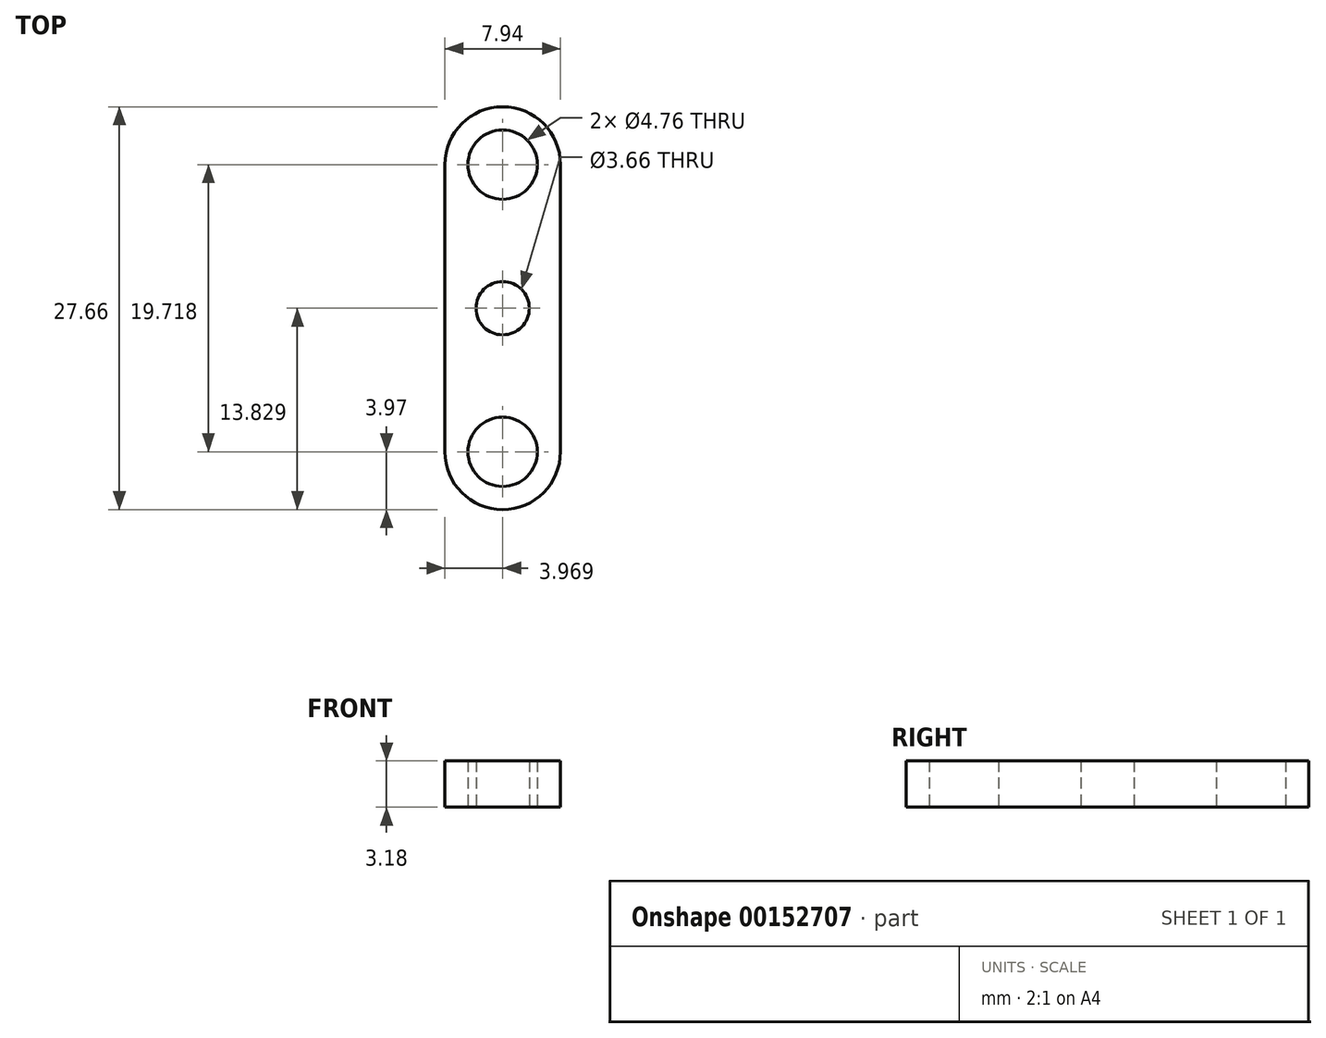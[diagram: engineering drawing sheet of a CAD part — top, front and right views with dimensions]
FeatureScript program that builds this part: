
annotation { "Feature Type Name" : "Feature", "Feature Type Description" : "" }
export const myFeature = defineFeature(function(context is Context, id is Id, definition is map)
    precondition{}
    {
        {
            var Q0;
            Q0=qCreatedBy(makeId("Top.planeOp"),FACE);
            var sketch = newSketch(context, id + "F0", { "sketchPlane" : qUnion([Q0])});
            skLineSegment(sketch, "E0.bottom", {"start": v(0, 0) * mm, "end": v(7.94, 0) * mm, "construction": true});
            skLineSegment(sketch, "E0.top", {"start": v(0, 19.72) * mm, "end": v(7.94, 19.72) * mm, "construction": true});
            skLineSegment(sketch, "E0.left", {"start": v(0, 0) * mm, "end": v(0, 19.72) * mm});
            skLineSegment(sketch, "E0.right", {"start": v(7.94, 0) * mm, "end": v(7.94, 19.72) * mm});
            skArc(sketch, "E1", {"start": v(7.94, 19.72) * mm, "mid": v(3.97, 23.69) * mm, "end": v(0, 19.72) * mm});
            skArc(sketch, "E2", {"start": v(0, 0) * mm, "mid": v(3.97, -3.97) * mm, "end": v(7.94, 0) * mm});
            skCircle(sketch, "E3", {"center": v(3.97, 19.72) * mm, "radius": 2.38 * mm});
            skCircle(sketch, "E4", {"center": v(3.97, 0) * mm, "radius": 2.38 * mm});
            skLineSegment(sketch, "E5", {"start": v(3.97, 19.72) * mm, "end": v(3.97, 0) * mm, "construction": true});
            skCircle(sketch, "E6", {"center": v(3.97, 9.86) * mm, "radius": 1.83 * mm});
            skSolve(sketch);
        }
        {
            var Q0;
            Q0=qSketchRegion(id+"F0",true);
            extrude(context, id + "F1", {"entities" : qUnion([Q0]), "depth" : 3.17 * mm});
        }
    });
